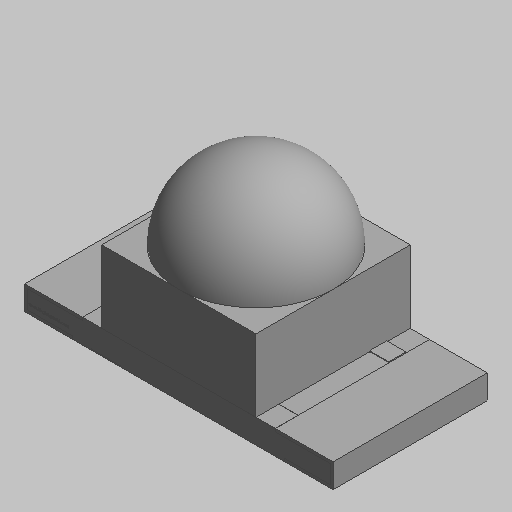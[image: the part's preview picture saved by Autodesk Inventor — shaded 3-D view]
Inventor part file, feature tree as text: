
AUTODESK INVENTOR PART (.ipt)
format: ipt  version: 2023.5 (Build 275446000, 446)  size: 552,960 bytes
history: native  units: mm (DEFAULTED — no unit token found)
features: extrude x7, revolve x1, other x1
ambient origin geometry x8: Origin, YZ Plane, XZ Plane, XY Plane, X Axis, Y Axis, Z Axis, Center Point
bodies: Solid1 (feature_tree), Solid2 (feature_tree), Solid3 (feature_tree), Solid4 (feature_tree), Solid5 (feature_tree), Solid6 (feature_tree), Solid7 (feature_tree), Solid8 (feature_tree), Solid9 (feature_tree)
feature tree (9):
  revolve  "Revolve1"  [1 undecoded]
  extrude  "Extrude2[1]"  [1 undecoded]
  extrude  "Extrude2[2]"  [1 undecoded]
  extrude  "Extrude3"  [1 undecoded]
  extrude  "Extrude4[1]"  [1 undecoded]
  extrude  "Extrude4[2]"  [1 undecoded]
  extrude  "Extrude6"  [1 undecoded]
  other  "Cut-Extrude1"
  extrude  "Extrude7"  [1 undecoded]
note: 8 required parameter values undecoded (feature->parameter linkage not recoverable at this tier; creation-order binding heuristic only, values carry confidence <= 0.55)
